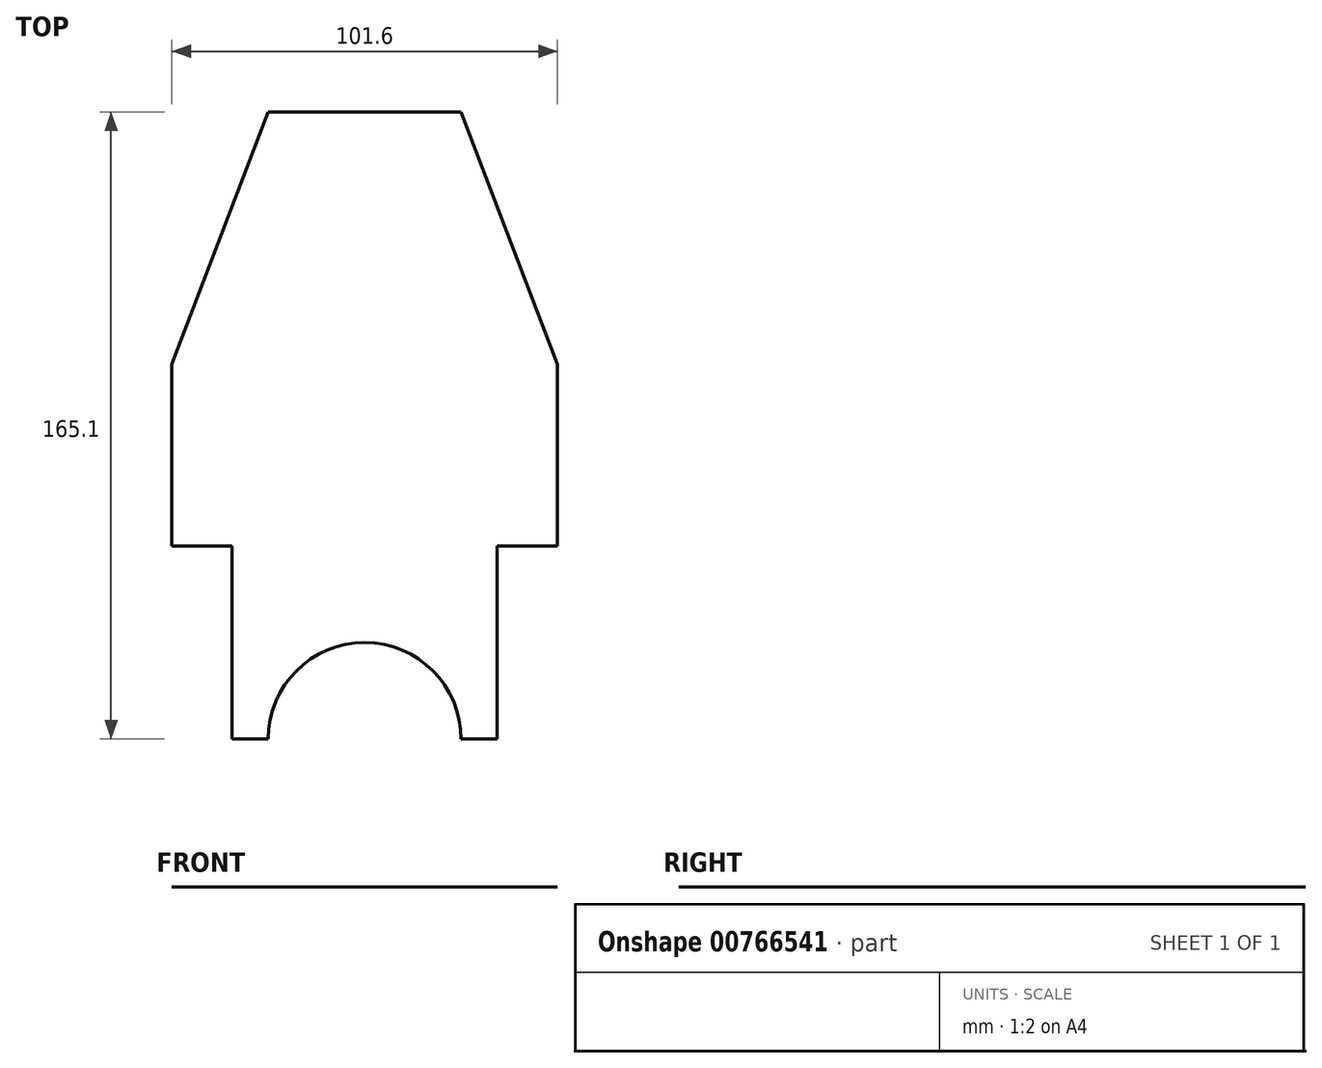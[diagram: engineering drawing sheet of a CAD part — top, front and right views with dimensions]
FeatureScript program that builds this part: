
annotation { "Feature Type Name" : "Feature", "Feature Type Description" : "" }
export const myFeature = defineFeature(function(context is Context, id is Id, definition is map)
    precondition{}
    {
        {
            var Q0;
            Q0=qCreatedBy(makeId("Top.planeOp"),FACE);
            var sketch = newSketch(context, id + "F0", { "sketchPlane" : qUnion([Q0])});
            skLineSegment(sketch, "E0.top", {"start": v(25.4, 66.48) * mm, "end": v(-25.4, 66.48) * mm});
            skLineSegment(sketch, "E0.left", {"start": v(50.8, -47.82) * mm, "end": v(50.8, 0) * mm});
            skLineSegment(sketch, "E0.right", {"start": v(-50.8, -47.82) * mm, "end": v(-50.8, 0) * mm});
            skPoint(sketch, "E0.middle", {"position": v(0, 0) * mm});
            skLineSegment(sketch, "E1", {"start": v(50.8, -47.82) * mm, "end": v(34.93, -47.82) * mm});
            skLineSegment(sketch, "E2", {"start": v(34.93, -47.82) * mm, "end": v(34.93, -98.62) * mm});
            skLineSegment(sketch, "E3", {"start": v(-34.93, -98.62) * mm, "end": v(-34.93, -47.82) * mm});
            skLineSegment(sketch, "E4", {"start": v(-34.93, -47.82) * mm, "end": v(-50.8, -47.82) * mm});
            skLineSegment(sketch, "E5", {"start": v(50.8, 0) * mm, "end": v(25.4, 66.48) * mm});
            skLineSegment(sketch, "E6", {"start": v(-25.4, 66.48) * mm, "end": v(-50.8, 0) * mm});
            skPoint(sketch, "E7", {"position": v(0, -98.62) * mm});
            skArc(sketch, "E8", {"start": v(25.4, -98.62) * mm, "mid": v(0, -73.22) * mm, "end": v(-25.4, -98.62) * mm});
            skLineSegment(sketch, "E9", {"start": v(25.4, -98.62) * mm, "end": v(34.93, -98.62) * mm});
            skLineSegment(sketch, "E10", {"start": v(-25.4, -98.62) * mm, "end": v(-34.93, -98.62) * mm});
            skPoint(sketch, "E11", {"position": v(-34.93, -76.4) * mm});
            skPoint(sketch, "E12", {"position": v(-50.8, -25.4) * mm});
            skPoint(sketch, "E13", {"position": v(-34.93, -55.4) * mm});
            skSolve(sketch);
        }
        {
            var Q0;
            Q0=makeQuery(id+"F0.imprint","IMPRINT",FACE,{"disambiguationData":[TD([[makeQuery(id+"F0.imprint","IMPRINT",EDGE,{"derivedFrom":sQuery(id+"F0.wireOp",EDGE,"E0.top")}),1.0]])]});
            extrude(context, id + "F1", {"entities" : qUnion([Q0]), "oppositeDirection" : true, "depth" : 1 / 203.2 * mm, "offsetDistance" : 25.4 * mm});
        }
    });
